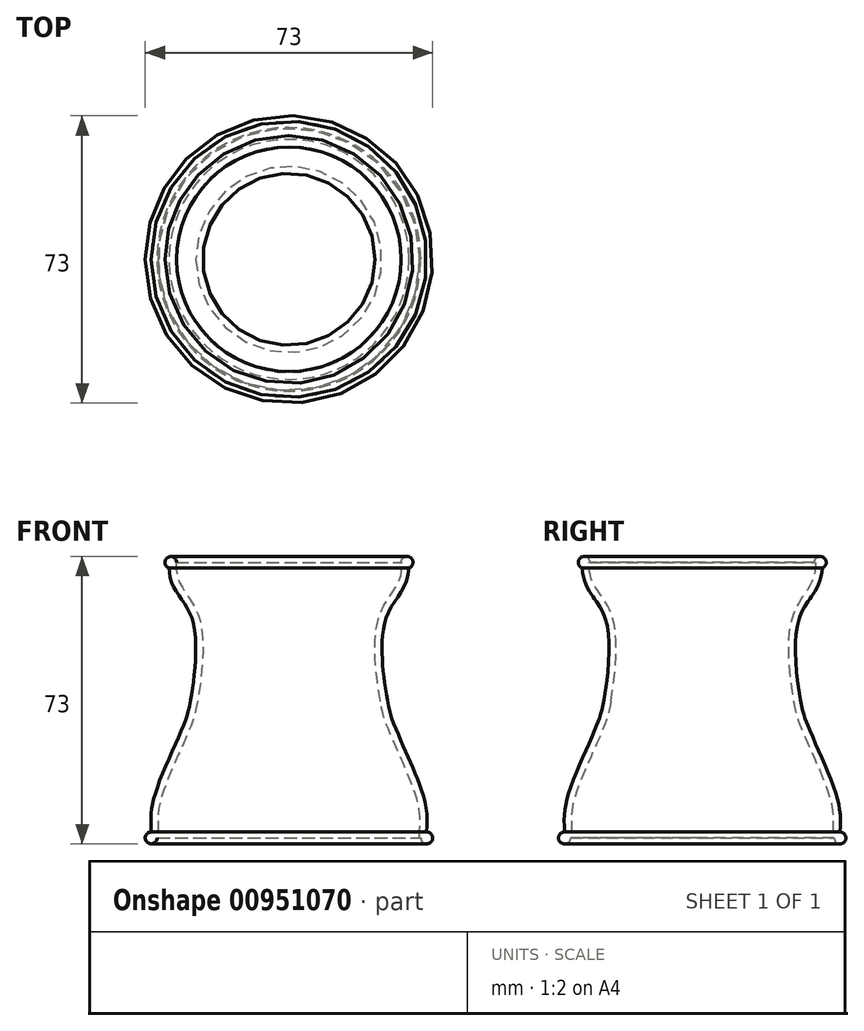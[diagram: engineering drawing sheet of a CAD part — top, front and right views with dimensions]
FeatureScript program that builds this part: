
annotation { "Feature Type Name" : "Feature", "Feature Type Description" : "" }
export const myFeature = defineFeature(function(context is Context, id is Id, definition is map)
    precondition{}
    {
        {
            var Q0;
            Q0=qCreatedBy(makeId("Front.planeOp"),FACE);
            var sketch = newSketch(context, id + "F0", { "sketchPlane" : qUnion([Q0])});
            skLineSegment(sketch, "E0", {"start": v(0, 0) * mm, "end": v(35, 0) * mm});
            skLineSegment(sketch, "E1", {"start": v(0, 0) * mm, "end": v(0, 70) * mm});
            skLineSegment(sketch, "E2", {"start": v(0, 70) * mm, "end": v(30, 70) * mm});
            skLineSegment(sketch, "E3", {"start": v(0, 35) * mm, "end": v(25, 35) * mm});
            skFitSpline(sketch, "E4", {"points": [v(35, 0) * mm, v(35, 6.55) * mm, v(32.82, 14.55) * mm, v(26.97, 28.17) * mm, v(25, 35) * mm, v(24.52, 55.4) * mm, v(29.96, 65.47) * mm, v(30, 70) * mm, v(30, 70) * mm], "startDerivative": vector(0, 83.95) * mm, "endDerivative": vector(37.37, 40.74) * mm});
            skCircle(sketch, "E5", {"center": v(30, 70) * mm, "radius": 1.5 * mm});
            skCircle(sketch, "E6", {"center": v(35, 0) * mm, "radius": 1.5 * mm});
            skSolve(sketch);
        }
        {
            var Q0;
            {var subQ0=sQuery(id+"F0.wireOp",EDGE,"E2");Q0=makeQuery(id+"F0.imprint","IMPRINT",FACE,{"disambiguationData":[TD([[makeQuery(id+"F0.imprint","IMPRINT",EDGE,{"derivedFrom":subQ0}),-1.0]])]});}
            var Q1;
            {var subQ0=sQuery(id+"F0.wireOp",EDGE,"E0");Q1=makeQuery(id+"F0.imprint","IMPRINT",FACE,{"disambiguationData":[TD([[makeQuery(id+"F0.imprint","IMPRINT",EDGE,{"derivedFrom":subQ0}),1.0]])]});}
            var Q2;
            {var subQ0=sQuery(id+"F0.wireOp",EDGE,"E3");Q2=makeQuery(id+"F0.imprint","IMPRINT",FACE,{"disambiguationData":[TD([[makeQuery(id+"F0.imprint","IMPRINT",EDGE,{"derivedFrom":subQ0}),1.0]])]});}
            var Q3;
            {var subQ0=sQuery(id+"F0.wireOp",EDGE,"E4");var subQ1=sQuery(id+"F0.wireOp",EDGE,"E2");var subQ2=makeQuery(id+"F0.imprint","INTERSECT",VERTEX,{"derivedFrom":[subQ1,subQ0]});Q3=makeQuery(id+"F0.imprint","IMPRINT",FACE,{"disambiguationData":[TD([[makeQuery(id+"F0.imprint","IMPRINT",EDGE,{"disambiguationData":[TD([[subQ2,1.0]])],"derivedFrom":subQ1}),1.0]])]});}
            var Q4;
            {var subQ1=sQuery(id+"F0.wireOp",EDGE,"E3");Q4=makeQuery(id+"F0.imprint","IMPRINT",FACE,{"disambiguationData":[TD([[makeQuery(id+"F0.imprint","IMPRINT",EDGE,{"derivedFrom":subQ1}),-1.0]])]});}
            var Q5;
            {var subQ0=sQuery(id+"F0.wireOp",EDGE,"E4");var subQ1=sQuery(id+"F0.wireOp",EDGE,"E0");var subQ2=makeQuery(id+"F0.imprint","INTERSECT",VERTEX,{"derivedFrom":[subQ1,subQ0]});Q5=makeQuery(id+"F0.imprint","IMPRINT",FACE,{"disambiguationData":[TD([[makeQuery(id+"F0.imprint","IMPRINT",EDGE,{"disambiguationData":[TD([[subQ2,1.0]])],"derivedFrom":subQ1}),-1.0]])]});}
            var Q6;
            Q6=sQuery(id+"F0.wireOp",EDGE,"E1");
            revolve(context, id + "F1", {"surfaceOperationType" : NewSurfaceOperationType.NEW, "entities" : qUnion([Q0, Q1, Q2, Q3, Q4, Q5]), "axis" : qUnion([Q6]), "revolveType" : RevolveType.FULL});
        }
        {
            var Q0;
            Q0=makeQuery(id+"F1.opRevolve","SWEPT_FACE",FACE,{"disambiguationData":[OSD([sQuery(id+"F0.wireOp",EDGE,"E2")])]});
            var Q1;
            Q1=makeQuery(id+"F1.opRevolve","SWEPT_FACE",FACE,{"disambiguationData":[OSD([sQuery(id+"F0.wireOp",EDGE,"E0")])]});
            shell(context, id + "F2", {"entities" : qUnion([Q0, Q1]), "thickness" : 1.8 * mm});
        }
    });
